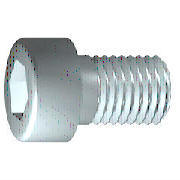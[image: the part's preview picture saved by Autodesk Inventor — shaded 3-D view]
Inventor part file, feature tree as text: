
AUTODESK INVENTOR PART (.ipt)
format: ipt  version: 2024.3 (Build 283343000, 343)  size: 183,808 bytes
history: native  units: mm (DEFAULTED — no unit token found)
features: extrude x1, plane x1, fillet x1
ambient origin geometry x7: Origin, YZ Plane, XY Plane, X Axis, Y Axis, Z Axis, Center Point
bodies: Solid1 (feature_tree), Body (feature_tree)
feature tree (3):
  extrude  "Slot"  Depth=19.0mm
  plane  "Work Plane1"
  fillet  "Fillet2"  Radius=0.24548mm
